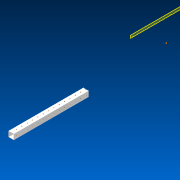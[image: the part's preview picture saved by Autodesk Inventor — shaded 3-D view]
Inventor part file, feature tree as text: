
AUTODESK INVENTOR PART (.ipt)
format: ipt  version: 2022.2 (Build 262287000, 287)  size: 832,512 bytes
history: native  units: in
note: dims shown in document units (in); Inventor stores cm internally (conversion verified against a paired STEP export)
features: other x28, extrude x2, pattern_linear x2, sketch x2
ambient origin geometry x8: Origin, YZ Plane, XZ Plane, XY Plane, X Axis, Y Axis, Z Axis, Center Point
bodies: Solid1 (feature_tree)
feature tree (34):
  extrude  "Extrusion1"  TaperAngle=0.0deg  [1 undecoded]
  other  "Work Axis1"
  other  "Work Axis2"
  pattern_linear  "Rectangular Pattern1"  Count1=14  [1 undecoded]
  pattern_linear  "Rectangular Pattern2"  Count1=13  [1 undecoded]
  extrude  "Extrusion2"  Depth=1.0in
  sketch  "Sketch1"  dims[d0=45.0in d1=0.0in d2=5.5118in]
  other  "Work Axis3"
  other  "Work Axis4"
  other  "Work Axis5"
  other  "Work Axis6"
  other  "Work Axis7"
  other  "Work Axis8"
  other  "Work Axis9"
  other  "Work Axis10"
  other  "Work Axis11"
  other  "Work Axis12"
  other  "Work Axis13"
  other  "Work Axis14"
  other  "Work Axis15"
  other  "Work Axis16"
  other  "Work Axis17"
  other  "Work Axis63"
  other  "Work Axis64"
  other  "Work Axis65"
  other  "Work Axis66"
  other  "Work Axis67"
  other  "Work Axis68"
  other  "Work Axis69"
  other  "Work Axis70"
  other  "Work Axis71"
  other  "Work Axis72"
  sketch  "Sketch2"  dims[d4=1.0in d5=5.1181in d7=1.0in d8=0.0in d9=0.0in]
  other  "LPattern2"
note: 3 required parameter values undecoded (feature->parameter linkage not recoverable at this tier; creation-order binding heuristic only, values carry confidence <= 0.55)
